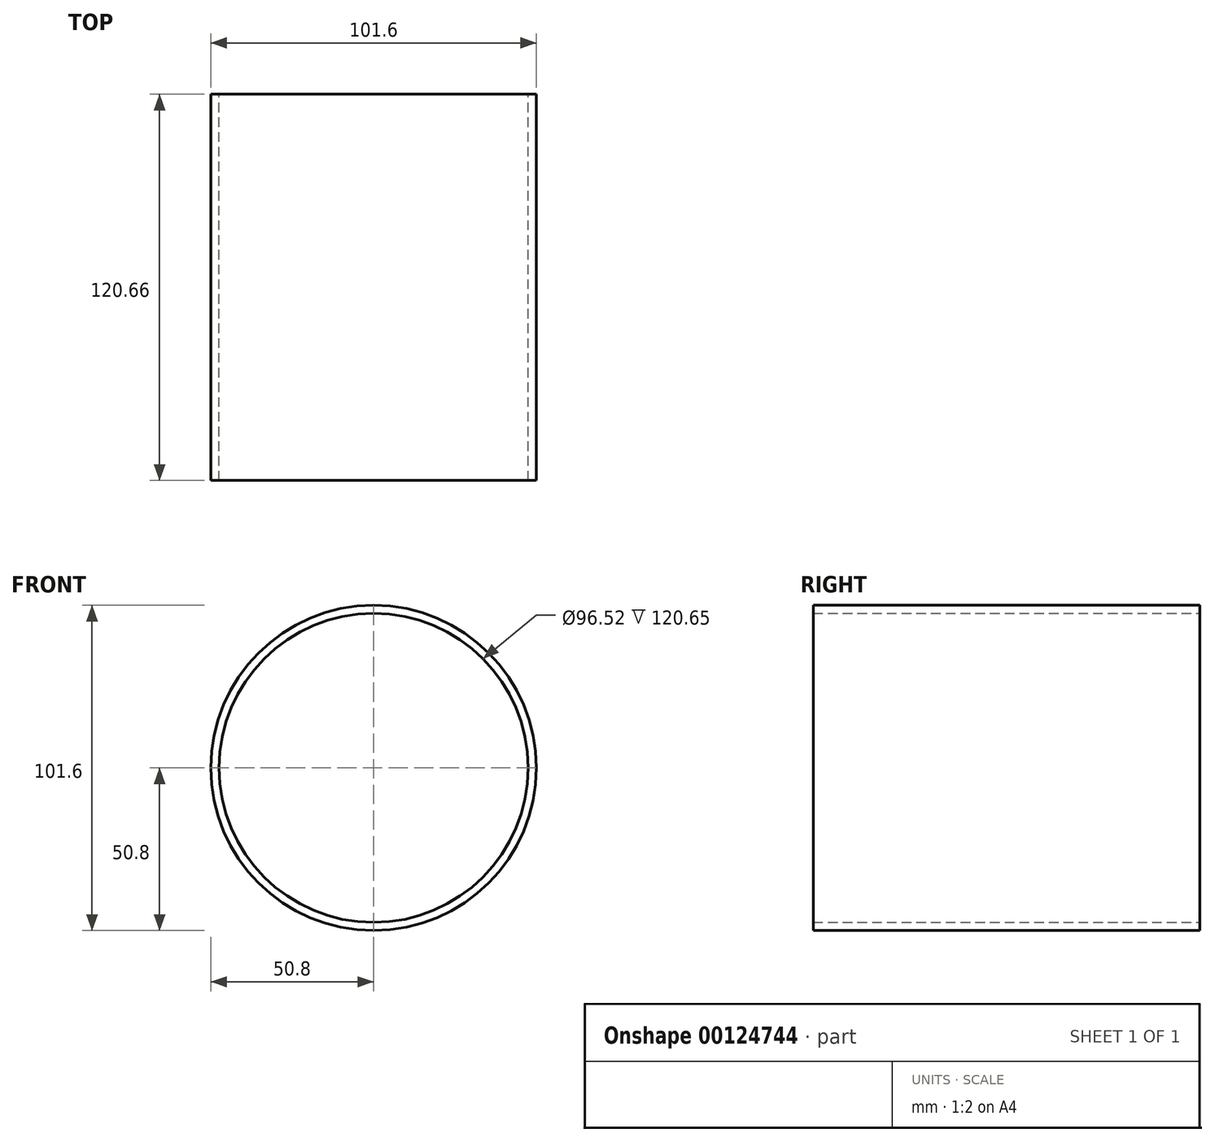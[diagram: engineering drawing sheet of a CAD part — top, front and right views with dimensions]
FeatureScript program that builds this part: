
annotation { "Feature Type Name" : "Feature", "Feature Type Description" : "" }
export const myFeature = defineFeature(function(context is Context, id is Id, definition is map)
    precondition{}
    {
        {
            var Q0;
            Q0=qCreatedBy(makeId("Front.planeOp"),FACE);
            var sketch = newSketch(context, id + "F0", { "sketchPlane" : qUnion([Q0])});
            skCircle(sketch, "E0", {"center": v(0, 0) * mm, "radius": 50.8 * mm});
            skSolve(sketch);
        }
        {
            var Q0;
            Q0 = qSketchRegion(id + "F0", true);
            var Q1;
            Q1=sQuery(id+"F0.wireOp",EDGE,"E0");
            extrude(context, id + "F1", {"entities" : qUnion([Q0]), "surfaceEntities" : qUnion([Q1]), "endBound" : BoundingType.SYMMETRIC, "depth" : 120.65 * mm});
        }
        {
            var Q0;
            Q0=makeQuery(id+"F1.opExtrude","CAP_FACE",FACE,{"disambiguationData":[OSD([sQuery(id+"F0.wireOp",EDGE,"E0")])],"isStart":true});
            var Q1;
            Q1=makeQuery(id+"F1.opExtrude","CAP_FACE",FACE,{"disambiguationData":[OSD([sQuery(id+"F0.wireOp",EDGE,"E0")])],"isStart":false});
            shell(context, id + "F2", {"entities" : qUnion([Q0, Q1]), "thickness" : 2.54 * mm});
        }
    });
